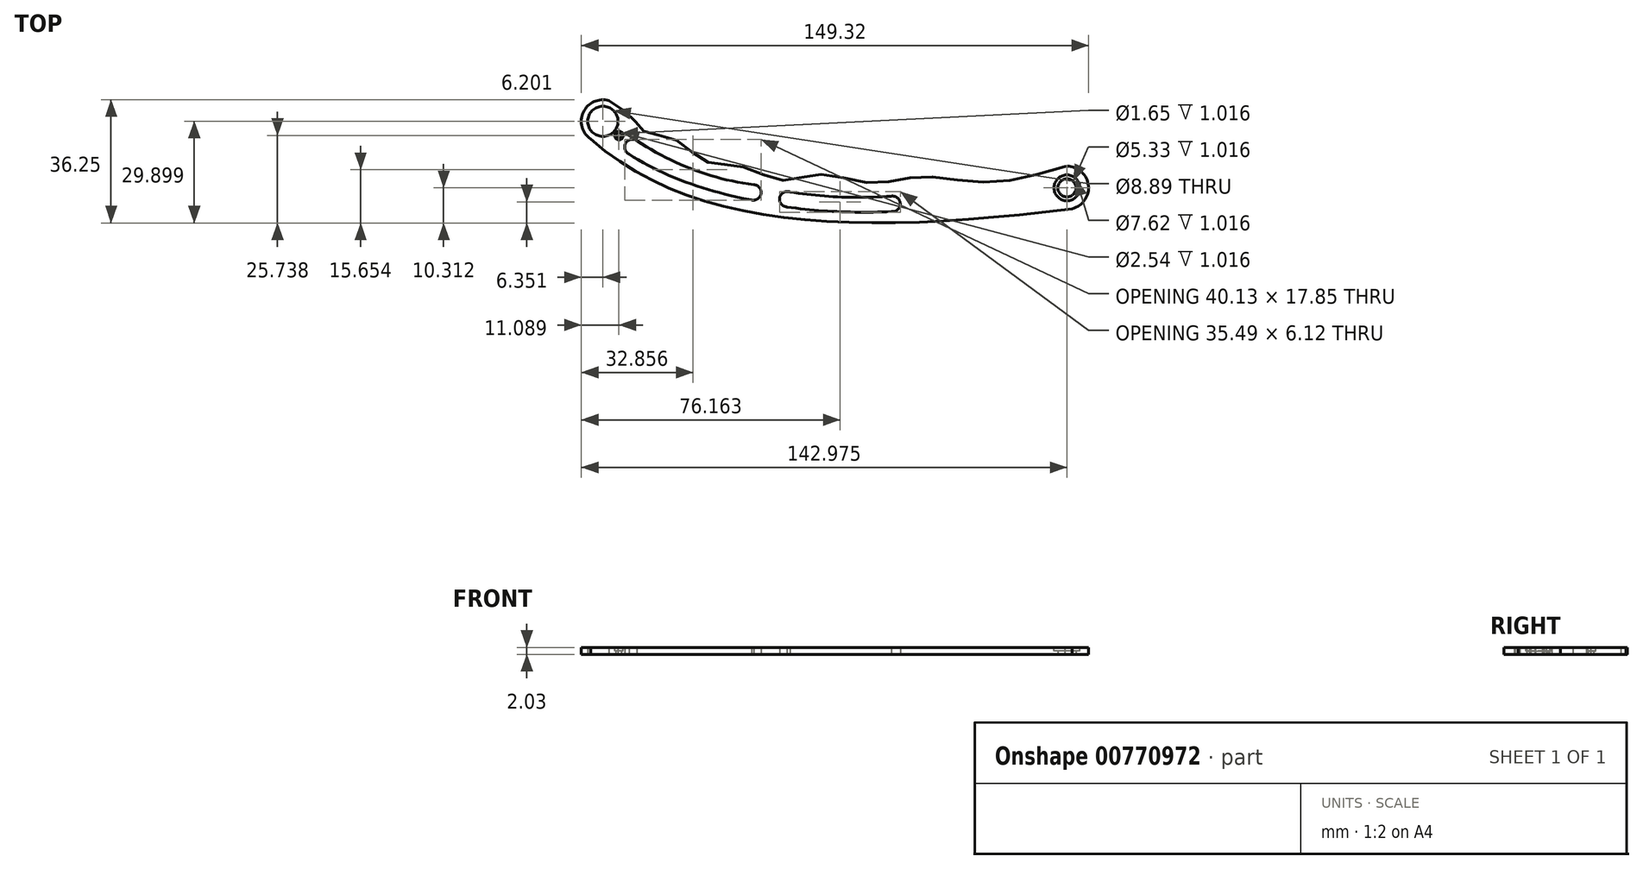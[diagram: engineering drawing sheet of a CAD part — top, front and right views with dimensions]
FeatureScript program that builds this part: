
annotation { "Feature Type Name" : "Feature", "Feature Type Description" : "" }
export const myFeature = defineFeature(function(context is Context, id is Id, definition is map)
    precondition{}
    {
        {
            var Q0;
            Q0=qCreatedBy(makeId("Top.planeOp"),FACE);
            var sketch = newSketch(context, id + "F0", { "sketchPlane" : qUnion([Q0])});
            skArc(sketch, "E0", {"start": v(-20.07, -47.23) * mm, "mid": v(-15.4, -39.99) * mm, "end": v(-22.25, -34.76) * mm});
            skArc(sketch, "E1", {"start": v(-156.48, -15.4) * mm, "mid": v(-164, -18.76) * mm, "end": v(-161.88, -26.72) * mm});
            skFitSpline(sketch, "E2", {"points": [v(-161.88, -26.72) * mm, v(-20.07, -47.23) * mm], "startDerivative": vector(94.28, -83.24) * mm, "endDerivative": vector(181.53, 22.33) * mm});
            skFitSpline(sketch, "E3", {"points": [v(-156.48, -15.4) * mm, v(-149.2, -20.87) * mm, v(-145.9, -24.58) * mm, v(-137.04, -26.85) * mm, v(-127.77, -33.45) * mm, v(-118.5, -34.48) * mm, v(-105.72, -38.8) * mm, v(-94.8, -37.16) * mm, v(-78.93, -39.63) * mm, v(-64.5, -37.78) * mm, v(-45.34, -39.43) * mm, v(-22.25, -34.76) * mm], "startDerivative": vector(108.37, -68.53) * mm, "endDerivative": vector(186.46, 55.9) * mm});
            skCircle(sketch, "E4", {"center": v(-21.65, -41.08) * mm, "radius": 2.67 * mm});
            skCircle(sketch, "E5", {"center": v(-158.27, -21.5) * mm, "radius": 4.45 * mm});
            skPoint(sketch, "E6.orphan", {"position": v(-142.4, -32.8) * mm});
            skArc(sketch, "E7", {"start": v(-148.23, -27.2) * mm, "mid": v(-151.51, -27.86) * mm, "end": v(-150.61, -31.09) * mm});
            skArc(sketch, "E8", {"start": v(-114.46, -44.65) * mm, "mid": v(-111.7, -42.75) * mm, "end": v(-113.78, -40.14) * mm});
            skArc(sketch, "E9", {"start": v(-103.12, -42.3) * mm, "mid": v(-106.2, -43.92) * mm, "end": v(-104.1, -46.7) * mm});
            skArc(sketch, "E10", {"start": v(-73.35, -48.05) * mm, "mid": v(-70.71, -45.78) * mm, "end": v(-73.37, -43.53) * mm});
            skFitSpline(sketch, "E11", {"points": [v(-104.1, -42.13) * mm, v(-72.96, -43.5) * mm], "startDerivative": vector(29.21, -4.98) * mm, "endDerivative": vector(31.97, 2.36) * mm});
            skFitSpline(sketch, "E12", {"points": [v(-104.1, -46.7) * mm, v(-73.35, -48.05) * mm], "startDerivative": vector(30.73, -4.4) * mm, "endDerivative": vector(30.8, 1.47) * mm});
            skFitSpline(sketch, "E13", {"points": [v(-148.4, -27.1) * mm, v(-113.57, -40.16) * mm], "startDerivative": vector(32.12, -21.1) * mm, "endDerivative": vector(38.06, -4.75) * mm});
            skFitSpline(sketch, "E14", {"points": [v(-150.61, -31.09) * mm, v(-114.46, -44.65) * mm], "startDerivative": vector(30.97, -20.7) * mm, "endDerivative": vector(35.39, -6.39) * mm});
            skSolve(sketch);
        }
        {
            var Q0;
            Q0=makeQuery(id+"F0.imprint","IMPRINT",FACE,{"disambiguationData":[TD([[makeQuery(id+"F0.imprint","IMPRINT",EDGE,{"derivedFrom":sQuery(id+"F0.wireOp",EDGE,"E0")}),1.0]])]});
            extrude(context, id + "F1", {"entities" : qUnion([Q0]), "depth" : 2.03 * mm, "offsetDistance" : 25.4 * mm});
        }
        {
            var Q0;
            Q0=makeQuery(id+"F1.opExtrude","CAP_FACE",FACE,{"disambiguationData":[OSD([sQuery(id+"F0.wireOp",EDGE,"E0"),sQuery(id+"F0.wireOp",EDGE,"E1"),sQuery(id+"F0.wireOp",EDGE,"E2"),sQuery(id+"F0.wireOp",EDGE,"E3"),sQuery(id+"F0.wireOp",EDGE,"E4"),sQuery(id+"F0.wireOp",EDGE,"E5"),sQuery(id+"F0.wireOp",EDGE,"E7"),sQuery(id+"F0.wireOp",EDGE,"E8"),sQuery(id+"F0.wireOp",EDGE,"E9"),sQuery(id+"F0.wireOp",EDGE,"E10"),sQuery(id+"F0.wireOp",EDGE,"E11"),sQuery(id+"F0.wireOp",EDGE,"E12"),sQuery(id+"F0.wireOp",EDGE,"E13"),sQuery(id+"F0.wireOp",EDGE,"E14")])],"isStart":false});
            var sketch = newSketch(context, id + "F2", { "sketchPlane" : qUnion([Q0])});
            skCircle(sketch, "E15", {"center": v(-21.65, -41.08) * mm, "radius": 3.81 * mm});
            skSolve(sketch);
        }
        {
            var Q0;
            Q0=makeQuery(id+"F2.imprint","IMPRINT",FACE,{"disambiguationData":[TD([[makeQuery(id+"F2.imprint","IMPRINT",EDGE,{"derivedFrom":sQuery(id+"F2.wireOp",EDGE,"E15")}),1.0]])]});
            extrude(context, id + "F3", {"entities" : qUnion([Q0]), "operationType" : NewBodyOperationType.REMOVE, "oppositeDirection" : true, "depth" : 1.02 * mm, "offsetDistance" : 25.4 * mm});
        }
        {
            var Q0;
            Q0=makeQuery(id+"F1.opExtrude","CAP_FACE",FACE,{"disambiguationData":[OSD([sQuery(id+"F0.wireOp",EDGE,"E0"),sQuery(id+"F0.wireOp",EDGE,"E1"),sQuery(id+"F0.wireOp",EDGE,"E2"),sQuery(id+"F0.wireOp",EDGE,"E3"),sQuery(id+"F0.wireOp",EDGE,"E4"),sQuery(id+"F0.wireOp",EDGE,"E5"),sQuery(id+"F0.wireOp",EDGE,"E7"),sQuery(id+"F0.wireOp",EDGE,"E8"),sQuery(id+"F0.wireOp",EDGE,"E9"),sQuery(id+"F0.wireOp",EDGE,"E10"),sQuery(id+"F0.wireOp",EDGE,"E11"),sQuery(id+"F0.wireOp",EDGE,"E12"),sQuery(id+"F0.wireOp",EDGE,"E13"),sQuery(id+"F0.wireOp",EDGE,"E14")])],"isStart":false});
            var sketch = newSketch(context, id + "F4", { "sketchPlane" : qUnion([Q0])});
            skCircle(sketch, "E16", {"center": v(-153.53, -25.65) * mm, "radius": 0.83 * mm});
            skSolve(sketch);
        }
        {
            var Q0;
            Q0=makeQuery(id+"F4.imprint","IMPRINT",FACE,{"disambiguationData":[TD([[makeQuery(id+"F4.imprint","IMPRINT",EDGE,{"derivedFrom":sQuery(id+"F4.wireOp",EDGE,"E16")}),1.0]])]});
            extrude(context, id + "F5", {"entities" : qUnion([Q0]), "operationType" : NewBodyOperationType.REMOVE, "oppositeDirection" : true, "depth" : 25.4 * mm, "offsetDistance" : 25.4 * mm});
        }
        {
            var Q0;
            Q0=makeQuery(id+"F1.opExtrude","CAP_FACE",FACE,{"disambiguationData":[OSD([sQuery(id+"F0.wireOp",EDGE,"E0"),sQuery(id+"F0.wireOp",EDGE,"E1"),sQuery(id+"F0.wireOp",EDGE,"E2"),sQuery(id+"F0.wireOp",EDGE,"E3"),sQuery(id+"F0.wireOp",EDGE,"E4"),sQuery(id+"F0.wireOp",EDGE,"E5"),sQuery(id+"F0.wireOp",EDGE,"E7"),sQuery(id+"F0.wireOp",EDGE,"E8"),sQuery(id+"F0.wireOp",EDGE,"E9"),sQuery(id+"F0.wireOp",EDGE,"E10"),sQuery(id+"F0.wireOp",EDGE,"E11"),sQuery(id+"F0.wireOp",EDGE,"E12"),sQuery(id+"F0.wireOp",EDGE,"E13"),sQuery(id+"F0.wireOp",EDGE,"E14")])],"isStart":false});
            var sketch = newSketch(context, id + "F6", { "sketchPlane" : qUnion([Q0])});
            skCircle(sketch, "E17", {"center": v(-153.53, -25.65) * mm, "radius": 1.27 * mm});
            skSolve(sketch);
        }
        {
            var Q0;
            Q0=makeQuery(id+"F6.imprint","IMPRINT",FACE,{"disambiguationData":[TD([[makeQuery(id+"F6.imprint","IMPRINT",EDGE,{"derivedFrom":sQuery(id+"F6.wireOp",EDGE,"E17")}),1.0]])]});
            extrude(context, id + "F7", {"entities" : qUnion([Q0]), "operationType" : NewBodyOperationType.REMOVE, "oppositeDirection" : true, "depth" : 1.02 * mm, "offsetDistance" : 25.4 * mm});
        }
    });
